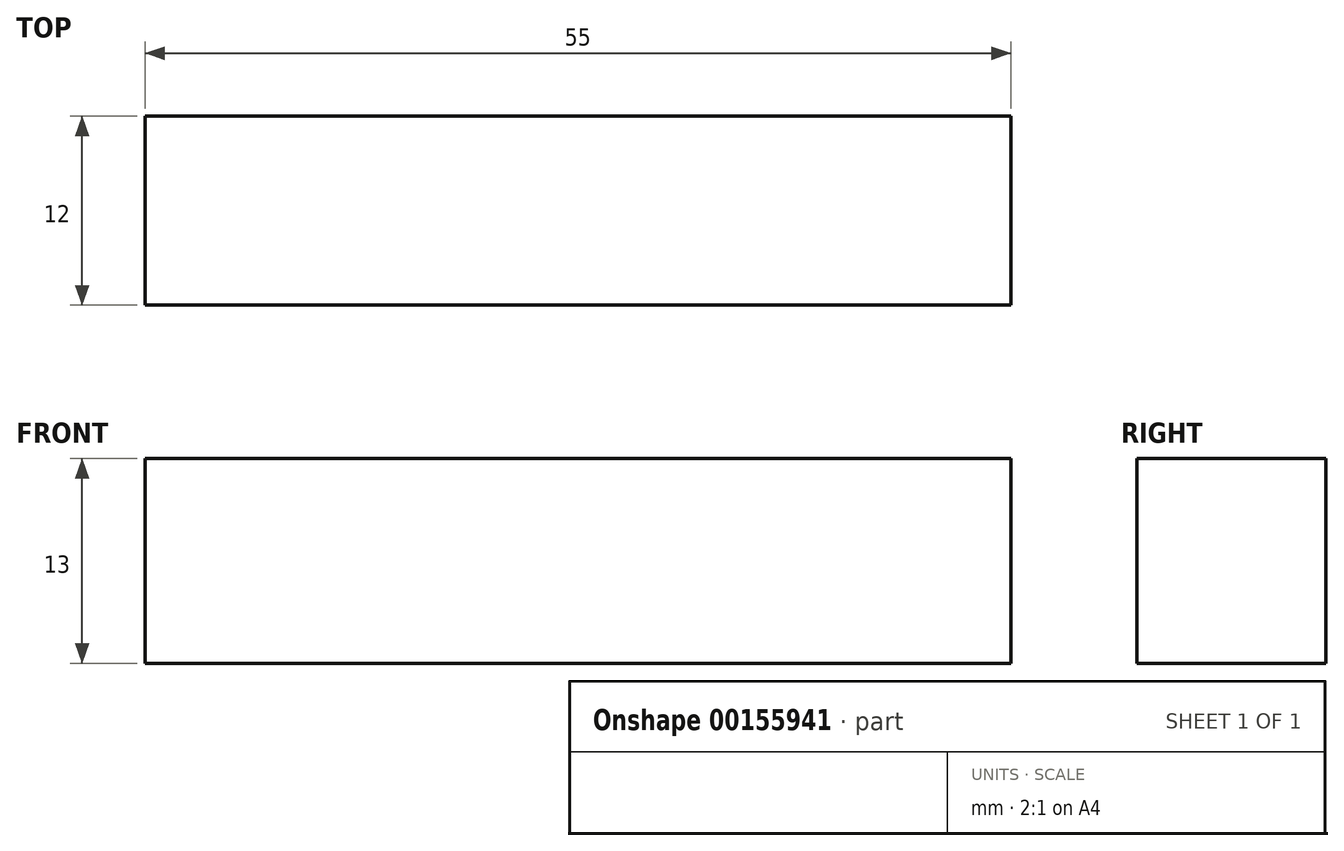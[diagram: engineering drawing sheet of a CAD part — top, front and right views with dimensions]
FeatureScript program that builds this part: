
annotation { "Feature Type Name" : "Feature", "Feature Type Description" : "" }
export const myFeature = defineFeature(function(context is Context, id is Id, definition is map)
    precondition{}
    {
        {
            var Q0;
            Q0=qCreatedBy(makeId("Front.planeOp"),FACE);
            var sketch = newSketch(context, id + "F0", { "sketchPlane" : qUnion([Q0])});
            skLineSegment(sketch, "E0.bottom", {"start": v(-66.2, 42.24) * mm, "end": v(-11.2, 42.24) * mm});
            skLineSegment(sketch, "E0.top", {"start": v(-66.2, 29.24) * mm, "end": v(-11.2, 29.24) * mm});
            skLineSegment(sketch, "E0.left", {"start": v(-66.2, 42.24) * mm, "end": v(-66.2, 29.24) * mm});
            skLineSegment(sketch, "E0.right", {"start": v(-11.2, 42.24) * mm, "end": v(-11.2, 29.24) * mm});
            skSolve(sketch);
        }
        {
            var Q0;
            Q0=makeQuery(id+"F0.imprint","IMPRINT",FACE,{"disambiguationData":[TD([[makeQuery(id+"F0.imprint","IMPRINT",EDGE,{"derivedFrom":sQuery(id+"F0.wireOp",EDGE,"E0.bottom")}),-1.0]])]});
            extrude(context, id + "F1", {"entities" : qUnion([Q0]), "oppositeDirection" : true, "depth" : 12 * mm});
        }
    });
